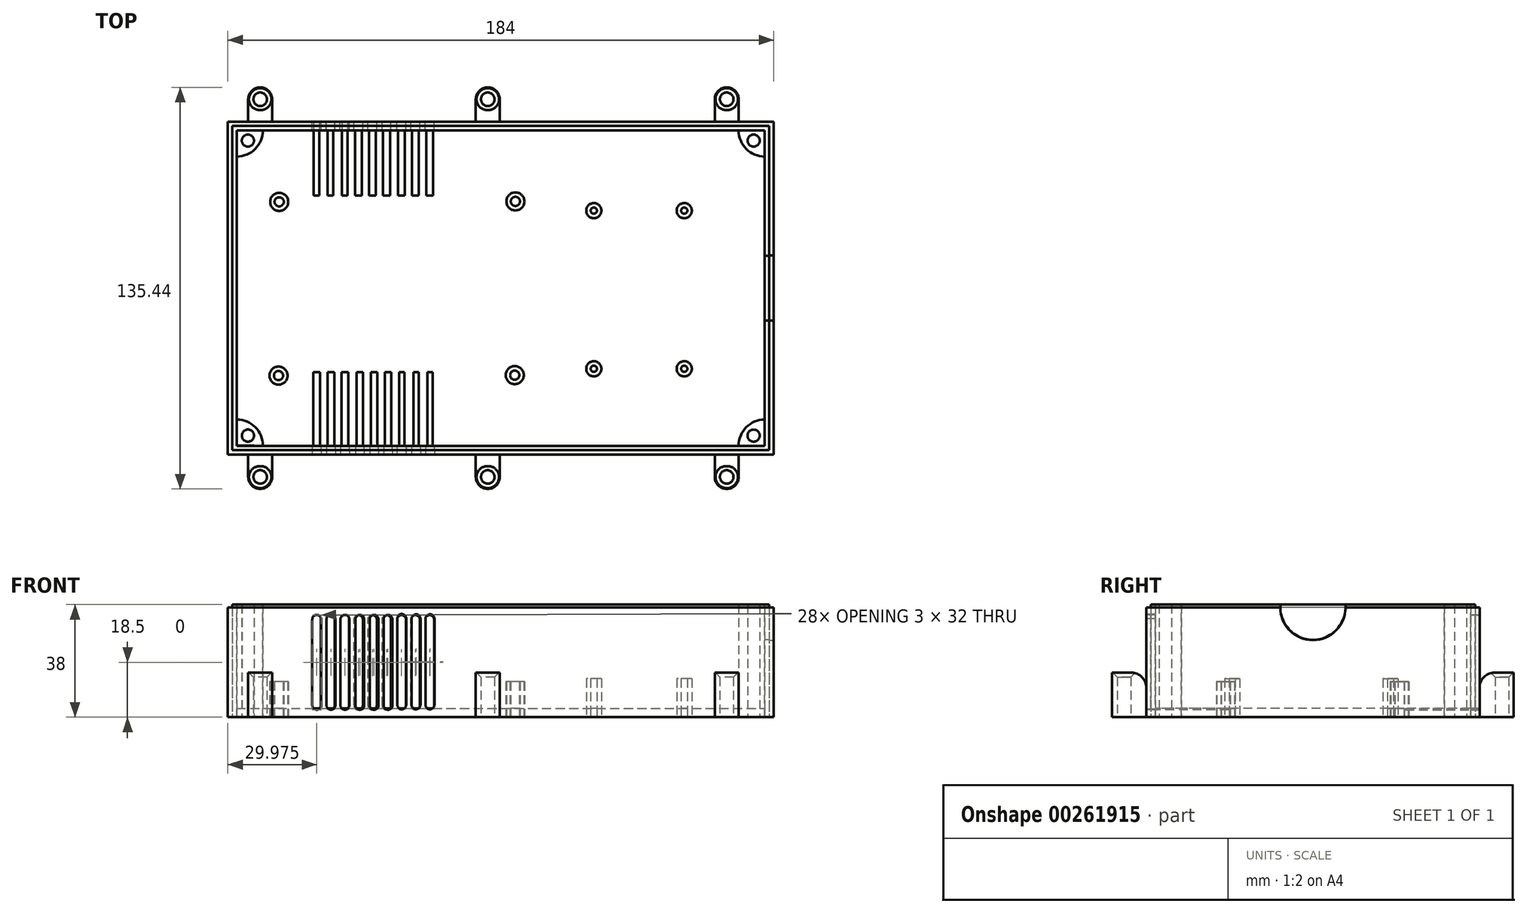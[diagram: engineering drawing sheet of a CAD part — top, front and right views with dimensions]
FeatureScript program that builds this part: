
annotation { "Feature Type Name" : "Feature", "Feature Type Description" : "" }
export const myFeature = defineFeature(function(context is Context, id is Id, definition is map)
    precondition{}
    {
        {
            var Q0;
            Q0=qCreatedBy(makeId("Top.planeOp"),FACE);
            var sketch = newSketch(context, id + "F0", { "sketchPlane" : qUnion([Q0])});
            skLineSegment(sketch, "E0.bottom", {"start": v(-92, 56.17) * mm, "end": v(92, 56.17) * mm});
            skLineSegment(sketch, "E0.top", {"start": v(-92, -56.17) * mm, "end": v(92, -56.17) * mm});
            skLineSegment(sketch, "E0.left", {"start": v(-92, 56.17) * mm, "end": v(-92, -56.17) * mm});
            skLineSegment(sketch, "E0.right", {"start": v(92, 56.17) * mm, "end": v(92, -56.17) * mm});
            skPoint(sketch, "E0.middle", {"position": v(0, 0) * mm});
            skLineSegment(sketch, "E1.0", {"start": v(-89, 53.17) * mm, "end": v(89, 53.17) * mm});
            skLineSegment(sketch, "E1.1", {"start": v(-89, 53.17) * mm, "end": v(-89, -53.17) * mm});
            skLineSegment(sketch, "E1.2", {"start": v(-89, -53.17) * mm, "end": v(89, -53.17) * mm});
            skLineSegment(sketch, "E1.3", {"start": v(89, 53.17) * mm, "end": v(89, -53.17) * mm});
            skLineSegment(sketch, "E2.0", {"start": v(-90.5, 54.67) * mm, "end": v(90.5, 54.67) * mm});
            skLineSegment(sketch, "E2.1", {"start": v(-90.5, 54.67) * mm, "end": v(-90.5, -54.67) * mm});
            skLineSegment(sketch, "E2.2", {"start": v(-90.5, -54.67) * mm, "end": v(90.5, -54.67) * mm});
            skLineSegment(sketch, "E2.3", {"start": v(90.5, 54.67) * mm, "end": v(90.5, -54.67) * mm});
            skSolve(sketch);
        }
        {
            var Q0;
            Q0=makeQuery(id+"F0.imprint","IMPRINT",FACE,{"disambiguationData":[TD([[makeQuery(id+"F0.imprint","IMPRINT",EDGE,{"derivedFrom":sQuery(id+"F0.wireOp",EDGE,"E1.0")}),-1.0]])]});
            var sketch = newSketch(context, id + "F1", { "sketchPlane" : qUnion([Q0])});
            skCircle(sketch, "E3", {"center": v(-85.23, 49.75) * mm, "radius": 2.05 * mm});
            skLineSegment(sketch, "E4", {"start": v(-83.13, 53.17) * mm, "end": v(-89, 53.17) * mm});
            skLineSegment(sketch, "E5", {"start": v(-89, 53.17) * mm, "end": v(-89, 50.23) * mm});
            skLineSegment(sketch, "E6.MirrorCS", {"start": v(-89, 47.29) * mm, "end": v(-89, 50.23) * mm});
            skLineSegment(sketch, "E7.MirrorCS", {"start": v(-89, 47.29) * mm, "end": v(-89, 44.34) * mm});
            skLineSegment(sketch, "E8", {"start": v(-80.2, 53.17) * mm, "end": v(-83.13, 53.17) * mm});
            skArc(sketch, "E9", {"start": v(-89, 44.34) * mm, "mid": v(-82.77, 46.94) * mm, "end": v(-80.2, 53.17) * mm});
            skLineSegment(sketch, "E10.MirrorCS", {"start": v(83.13, 53.17) * mm, "end": v(89, 53.17) * mm});
            skCircle(sketch, "E11.MirrorC", {"center": v(85.23, 49.75) * mm, "radius": 2.05 * mm});
            skLineSegment(sketch, "E12.MirrorCS", {"start": v(89, 53.17) * mm, "end": v(89, 50.23) * mm});
            skLineSegment(sketch, "E13.MirrorCS", {"start": v(80.2, 53.17) * mm, "end": v(83.13, 53.17) * mm});
            skLineSegment(sketch, "E14.MirrorCS", {"start": v(89, 47.29) * mm, "end": v(89, 50.23) * mm});
            skLineSegment(sketch, "E15.MirrorCS", {"start": v(89, 47.29) * mm, "end": v(89, 44.34) * mm});
            skArc(sketch, "E16.MirrorCS", {"start": v(89, 44.34) * mm, "mid": v(82.77, 46.94) * mm, "end": v(80.2, 53.17) * mm});
            skLineSegment(sketch, "E17.MirrorCS", {"start": v(-88.98, -53.17) * mm, "end": v(-88.98, -50.22) * mm});
            skLineSegment(sketch, "E18.MirrorCS", {"start": v(-88.98, -47.28) * mm, "end": v(-88.98, -50.22) * mm});
            skLineSegment(sketch, "E19.MirrorCS", {"start": v(-88.98, -47.28) * mm, "end": v(-88.98, -44.34) * mm});
            skLineSegment(sketch, "E20.MirrorCS", {"start": v(-80.17, -53.17) * mm, "end": v(-83.1, -53.17) * mm});
            skLineSegment(sketch, "E21.MirrorCS", {"start": v(80.2, -53.17) * mm, "end": v(83.13, -53.17) * mm});
            skLineSegment(sketch, "E22.MirrorCS", {"start": v(89, -53.17) * mm, "end": v(89, -50.23) * mm});
            skLineSegment(sketch, "E23.MirrorCS", {"start": v(89, -47.29) * mm, "end": v(89, -50.23) * mm});
            skLineSegment(sketch, "E24.MirrorCS", {"start": v(89, -47.29) * mm, "end": v(89, -44.34) * mm});
            skCircle(sketch, "E25.MirrorC", {"center": v(85.23, -49.75) * mm, "radius": 2.05 * mm});
            skLineSegment(sketch, "E26.MirrorCS", {"start": v(-83.1, -53.17) * mm, "end": v(-88.98, -53.17) * mm});
            skLineSegment(sketch, "E27.MirrorCS", {"start": v(83.13, -53.17) * mm, "end": v(89, -53.17) * mm});
            skArc(sketch, "E28.MirrorCS", {"start": v(89, -44.34) * mm, "mid": v(82.77, -46.94) * mm, "end": v(80.2, -53.17) * mm});
            skArc(sketch, "E29.MirrorCS", {"start": v(-88.98, -44.34) * mm, "mid": v(-82.75, -46.93) * mm, "end": v(-80.17, -53.17) * mm});
            skCircle(sketch, "E30.MirrorC", {"center": v(-85.21, -49.75) * mm, "radius": 2.05 * mm});
            skSolve(sketch);
        }
        {
            var Q0;
            Q0=makeQuery(id+"F0.imprint","IMPRINT",FACE,{"disambiguationData":[TD([[makeQuery(id+"F0.imprint","IMPRINT",EDGE,{"derivedFrom":sQuery(id+"F0.wireOp",EDGE,"E1.0")}),-1.0]])]});
            var sketch = newSketch(context, id + "F2", { "sketchPlane" : qUnion([Q0])});
            skLineSegment(sketch, "E31", {"start": v(-85.12, 56.17) * mm, "end": v(-85.12, 63.69) * mm});
            skLineSegment(sketch, "E32", {"start": v(-77.06, 63.69) * mm, "end": v(-77.06, 56.17) * mm});
            skArc(sketch, "E33", {"start": v(-77.06, 63.69) * mm, "mid": v(-81.09, 67.72) * mm, "end": v(-85.12, 63.69) * mm});
            skCircle(sketch, "E34", {"center": v(-81.09, 63.69) * mm, "radius": 2.28 * mm});
            skLineSegment(sketch, "E35", {"start": v(72.14, 56.17) * mm, "end": v(72.14, 63.69) * mm});
            skLineSegment(sketch, "E36", {"start": v(80.2, 63.69) * mm, "end": v(80.2, 56.17) * mm});
            skArc(sketch, "E37", {"start": v(80.2, 63.69) * mm, "mid": v(76.16, 67.72) * mm, "end": v(72.14, 63.69) * mm});
            skCircle(sketch, "E38", {"center": v(76.16, 63.69) * mm, "radius": 2.28 * mm});
            skLineSegment(sketch, "E39", {"start": v(-77.06, -56.17) * mm, "end": v(-77.06, -63.69) * mm});
            skLineSegment(sketch, "E40", {"start": v(-85.12, -63.69) * mm, "end": v(-85.12, -56.17) * mm});
            skArc(sketch, "E41", {"start": v(-85.12, -63.69) * mm, "mid": v(-81.09, -67.72) * mm, "end": v(-77.06, -63.69) * mm});
            skCircle(sketch, "E42", {"center": v(-81.09, -63.69) * mm, "radius": 2.28 * mm});
            skLineSegment(sketch, "E43", {"start": v(80.2, -56.17) * mm, "end": v(80.2, -63.69) * mm});
            skLineSegment(sketch, "E44", {"start": v(72.14, -63.69) * mm, "end": v(72.14, -56.17) * mm});
            skArc(sketch, "E45", {"start": v(72.14, -63.69) * mm, "mid": v(76.16, -67.72) * mm, "end": v(80.2, -63.69) * mm});
            skCircle(sketch, "E46", {"center": v(76.16, -63.69) * mm, "radius": 2.28 * mm});
            skLineSegment(sketch, "E47", {"start": v(-85.12, 56.17) * mm, "end": v(-77.06, 56.17) * mm});
            skLineSegment(sketch, "E48", {"start": v(72.14, 56.17) * mm, "end": v(80.2, 56.17) * mm});
            skLineSegment(sketch, "E49", {"start": v(72.14, -56.17) * mm, "end": v(80.2, -56.17) * mm});
            skLineSegment(sketch, "E50", {"start": v(-85.12, -56.17) * mm, "end": v(-77.06, -56.17) * mm});
            skLineSegment(sketch, "E51", {"start": v(-8.4, 56.17) * mm, "end": v(-8.4, 63.69) * mm});
            skLineSegment(sketch, "E52", {"start": v(-0.35, 63.69) * mm, "end": v(-0.35, 56.17) * mm});
            skArc(sketch, "E53", {"start": v(-0.35, 63.69) * mm, "mid": v(-4.37, 67.72) * mm, "end": v(-8.4, 63.69) * mm});
            skCircle(sketch, "E54", {"center": v(-4.37, 63.69) * mm, "radius": 2.28 * mm});
            skLineSegment(sketch, "E55", {"start": v(-0.35, -56.17) * mm, "end": v(-0.35, -63.69) * mm});
            skLineSegment(sketch, "E56", {"start": v(-8.4, -63.69) * mm, "end": v(-8.4, -56.17) * mm});
            skArc(sketch, "E57", {"start": v(-8.4, -63.69) * mm, "mid": v(-4.37, -67.72) * mm, "end": v(-0.35, -63.69) * mm});
            skCircle(sketch, "E58", {"center": v(-4.37, -63.69) * mm, "radius": 2.28 * mm});
            skLineSegment(sketch, "E59", {"start": v(-8.4, 56.17) * mm, "end": v(-0.35, 56.17) * mm});
            skLineSegment(sketch, "E60", {"start": v(-8.4, -56.17) * mm, "end": v(-0.35, -56.17) * mm});
            skSolve(sketch);
        }
        {
            var Q0;
            Q0=makeQuery(id+"F0.imprint","IMPRINT",FACE,{"disambiguationData":[TD([[makeQuery(id+"F0.imprint","IMPRINT",EDGE,{"derivedFrom":sQuery(id+"F0.wireOp",EDGE,"E1.0")}),-1.0]])]});
            var sketch = newSketch(context, id + "F3", { "sketchPlane" : qUnion([Q0])});
            skCircle(sketch, "E61", {"center": v(-74.92, -29.5) * mm, "radius": 1.55 * mm});
            skCircle(sketch, "E62", {"center": v(-74.68, 29.1) * mm, "radius": 1.55 * mm});
            skCircle(sketch, "E63", {"center": v(4.94, 29.25) * mm, "radius": 1.55 * mm});
            skCircle(sketch, "E64", {"center": v(4.7, -29.35) * mm, "radius": 1.55 * mm});
            skCircle(sketch, "E65.0", {"center": v(-74.92, -29.5) * mm, "radius": 3.05 * mm});
            skCircle(sketch, "E66.0", {"center": v(-74.68, 29.1) * mm, "radius": 3.05 * mm});
            skCircle(sketch, "E67.0", {"center": v(4.7, -29.35) * mm, "radius": 3.05 * mm});
            skCircle(sketch, "E68.0", {"center": v(4.94, 29.25) * mm, "radius": 3.05 * mm});
            skSolve(sketch);
        }
        {
            var Q0;
            Q0 = qSketchRegion(id + "F3", true);
            extrude(context, id + "F4", {"entities" : qUnion([Q0]), "depth" : 12 * mm});
        }
        {
            var Q0;
            Q0=makeQuery(id+"F3.imprint","IMPRINT",FACE,{"disambiguationData":[TD([[makeQuery(id+"F3.imprint","IMPRINT",EDGE,{"derivedFrom":sQuery(id+"F3.wireOp",EDGE,"E62")}),1.0]])]});
            var Q1;
            Q1=makeQuery(id+"F3.imprint","IMPRINT",FACE,{"disambiguationData":[TD([[makeQuery(id+"F3.imprint","IMPRINT",EDGE,{"derivedFrom":sQuery(id+"F3.wireOp",EDGE,"E63")}),1.0]])]});
            var Q2;
            Q2=makeQuery(id+"F3.imprint","IMPRINT",FACE,{"disambiguationData":[TD([[makeQuery(id+"F3.imprint","IMPRINT",EDGE,{"derivedFrom":sQuery(id+"F3.wireOp",EDGE,"E61")}),1.0]])]});
            var Q3;
            Q3=makeQuery(id+"F3.imprint","IMPRINT",FACE,{"disambiguationData":[TD([[makeQuery(id+"F3.imprint","IMPRINT",EDGE,{"derivedFrom":sQuery(id+"F3.wireOp",EDGE,"E64")}),1.0]])]});
            extrude(context, id + "F5", {"entities" : qUnion([Q0, Q1, Q2, Q3]), "depth" : 3 * mm});
        }
        {
            var Q0;
            Q0=makeQuery(id+"F0.imprint","IMPRINT",FACE,{"disambiguationData":[TD([[makeQuery(id+"F0.imprint","IMPRINT",EDGE,{"derivedFrom":sQuery(id+"F0.wireOp",EDGE,"E1.0")}),-1.0]])]});
            var sketch = newSketch(context, id + "F6", { "sketchPlane" : qUnion([Q0])});
            skCircle(sketch, "E69", {"center": v(31.37, 26.14) * mm, "radius": 1.05 * mm});
            skCircle(sketch, "E70", {"center": v(61.85, 26.14) * mm, "radius": 1.05 * mm});
            skCircle(sketch, "E71", {"center": v(61.85, -27.2) * mm, "radius": 1.05 * mm});
            skCircle(sketch, "E72", {"center": v(31.37, -27.2) * mm, "radius": 1.05 * mm});
            skCircle(sketch, "E73.0", {"center": v(31.37, 26.14) * mm, "radius": 2.55 * mm});
            skCircle(sketch, "E74.0", {"center": v(61.85, 26.14) * mm, "radius": 2.55 * mm});
            skCircle(sketch, "E75.0", {"center": v(31.37, -27.2) * mm, "radius": 2.55 * mm});
            skCircle(sketch, "E76.0", {"center": v(61.85, -27.2) * mm, "radius": 2.55 * mm});
            skSolve(sketch);
        }
        {
            var Q0;
            Q0=makeQuery(id+"F0.imprint","IMPRINT",FACE,{"disambiguationData":[TD([[makeQuery(id+"F0.imprint","IMPRINT",EDGE,{"derivedFrom":sQuery(id+"F0.wireOp",EDGE,"E0.bottom")}),-1.0]])]});
            extrude(context, id + "F7", {"entities" : qUnion([Q0]), "depth" : 37 * mm});
        }
        {
            var Q0;
            Q0=makeQuery(id+"F2.imprint","IMPRINT",FACE,{"disambiguationData":[TD([[makeQuery(id+"F2.imprint","IMPRINT",EDGE,{"derivedFrom":sQuery(id+"F2.wireOp",EDGE,"E31")}),-1.0]])]});
            var Q1;
            Q1=makeQuery(id+"F2.imprint","IMPRINT",FACE,{"disambiguationData":[TD([[makeQuery(id+"F2.imprint","IMPRINT",EDGE,{"derivedFrom":sQuery(id+"F2.wireOp",EDGE,"E35")}),-1.0]])]});
            var Q2;
            Q2=makeQuery(id+"F2.imprint","IMPRINT",FACE,{"disambiguationData":[TD([[makeQuery(id+"F2.imprint","IMPRINT",EDGE,{"derivedFrom":sQuery(id+"F2.wireOp",EDGE,"E39")}),-1.0]])]});
            var Q3;
            Q3=makeQuery(id+"F2.imprint","IMPRINT",FACE,{"disambiguationData":[TD([[makeQuery(id+"F2.imprint","IMPRINT",EDGE,{"derivedFrom":sQuery(id+"F2.wireOp",EDGE,"E43")}),-1.0]])]});
            var Q4;
            Q4=makeQuery(id+"F2.imprint","IMPRINT",FACE,{"disambiguationData":[TD([[makeQuery(id+"F2.imprint","IMPRINT",EDGE,{"derivedFrom":sQuery(id+"F2.wireOp",EDGE,"E55")}),-1.0]])]});
            var Q5;
            Q5=makeQuery(id+"F2.imprint","IMPRINT",FACE,{"disambiguationData":[TD([[makeQuery(id+"F2.imprint","IMPRINT",EDGE,{"derivedFrom":sQuery(id+"F2.wireOp",EDGE,"E51")}),-1.0]])]});
            extrude(context, id + "F8", {"entities" : qUnion([Q0, Q1, Q2, Q3, Q4, Q5]), "operationType" : NewBodyOperationType.ADD, "depth" : 15 * mm});
        }
        {
            var Q0;
            Q0=makeQuery(id+"F8.opExtrude","CAP_EDGE",EDGE,{"disambiguationData":[OSD([sQuery(id+"F2.wireOp",EDGE,"E34")])],"isStart":false});
            var Q1;
            Q1=makeQuery(id+"F8.opExtrude","CAP_EDGE",EDGE,{"disambiguationData":[OSD([sQuery(id+"F2.wireOp",EDGE,"E38")])],"isStart":false});
            var Q2;
            Q2=makeQuery(id+"F8.opExtrude","CAP_EDGE",EDGE,{"disambiguationData":[OSD([sQuery(id+"F2.wireOp",EDGE,"E46")])],"isStart":false});
            var Q3;
            Q3=makeQuery(id+"F8.opExtrude","CAP_EDGE",EDGE,{"disambiguationData":[OSD([sQuery(id+"F2.wireOp",EDGE,"E42")])],"isStart":false});
            var Q4;
            Q4=makeQuery(id+"F8.opExtrude","CAP_EDGE",EDGE,{"disambiguationData":[OSD([sQuery(id+"F2.wireOp",EDGE,"E54")])],"isStart":false});
            var Q5;
            Q5=makeQuery(id+"F8.opExtrude","CAP_EDGE",EDGE,{"disambiguationData":[OSD([sQuery(id+"F2.wireOp",EDGE,"E58")])],"isStart":false});
            chamfer(context, id + "F9", {"entities" : qUnion([Q0, Q1, Q2, Q3, Q4, Q5]), "width" : 1.5 * mm, "tangentPropagation" : true});
        }
        {
            var Q0;
            Q0=makeQuery(id+"F6.imprint","IMPRINT",FACE,{"disambiguationData":[TD([[makeQuery(id+"F6.imprint","IMPRINT",EDGE,{"derivedFrom":sQuery(id+"F6.wireOp",EDGE,"E72")}),1.0]])]});
            var Q1;
            Q1=makeQuery(id+"F6.imprint","IMPRINT",FACE,{"disambiguationData":[TD([[makeQuery(id+"F6.imprint","IMPRINT",EDGE,{"derivedFrom":sQuery(id+"F6.wireOp",EDGE,"E71")}),1.0]])]});
            var Q2;
            Q2=makeQuery(id+"F6.imprint","IMPRINT",FACE,{"disambiguationData":[TD([[makeQuery(id+"F6.imprint","IMPRINT",EDGE,{"derivedFrom":sQuery(id+"F6.wireOp",EDGE,"E69")}),1.0]])]});
            var Q3;
            Q3=makeQuery(id+"F6.imprint","IMPRINT",FACE,{"disambiguationData":[TD([[makeQuery(id+"F6.imprint","IMPRINT",EDGE,{"derivedFrom":sQuery(id+"F6.wireOp",EDGE,"E70")}),1.0]])]});
            var Q4;
            Q4=sQuery(id+"F6.wireOp",EDGE,"E72");
            var Q5;
            Q5=sQuery(id+"F6.wireOp",EDGE,"E71");
            var Q6;
            Q6=sQuery(id+"F6.wireOp",EDGE,"E70");
            var Q7;
            Q7=sQuery(id+"F6.wireOp",EDGE,"E69");
            extrude(context, id + "F10", {"entities" : qUnion([Q0, Q1, Q2, Q3]), "surfaceEntities" : qUnion([Q4, Q5, Q6, Q7]), "depth" : 3 * mm});
        }
        {
            var Q0;
            Q0 = qSketchRegion(id + "F6", true);
            extrude(context, id + "F11", {"entities" : qUnion([Q0]), "depth" : 13 * mm});
        }
        {
            var Q0;
            Q0=makeQuery(id+"F0.imprint","IMPRINT",FACE,{"disambiguationData":[TD([[makeQuery(id+"F0.imprint","IMPRINT",EDGE,{"derivedFrom":sQuery(id+"F0.wireOp",EDGE,"E1.0")}),-1.0]])]});
            extrude(context, id + "F12", {"entities" : qUnion([Q0]), "depth" : 3 * mm});
        }
        {
            var Q0;
            Q0=makeQuery(id+"F8.opExtrude","CAP_EDGE",EDGE,{"disambiguationData":[OSD([sQuery(id+"F2.wireOp",EDGE,"E48")])],"isStart":false});
            var Q1;
            Q1=makeQuery(id+"F8.boolean.opBoolean","INTERSECT",EDGE,{"derivedFrom":[makeQuery(id+"F7.opExtrude","SWEPT_FACE",FACE,{"disambiguationData":[OSD([sQuery(id+"F0.wireOp",EDGE,"E0.bottom")])]}),makeQuery(id+"F8.opExtrude","CAP_FACE",FACE,{"disambiguationData":[OSD([sQuery(id+"F2.wireOp",EDGE,"E31"),sQuery(id+"F2.wireOp",EDGE,"E32"),sQuery(id+"F2.wireOp",EDGE,"E33"),sQuery(id+"F2.wireOp",EDGE,"E34"),sQuery(id+"F2.wireOp",EDGE,"E47")])],"isStart":false})]});
            var Q2;
            Q2=makeQuery(id+"F8.boolean.opBoolean","INTERSECT",EDGE,{"derivedFrom":[makeQuery(id+"F7.opExtrude","SWEPT_FACE",FACE,{"disambiguationData":[OSD([sQuery(id+"F0.wireOp",EDGE,"E0.top")])]}),makeQuery(id+"F8.opExtrude","CAP_FACE",FACE,{"disambiguationData":[OSD([sQuery(id+"F2.wireOp",EDGE,"E39"),sQuery(id+"F2.wireOp",EDGE,"E40"),sQuery(id+"F2.wireOp",EDGE,"E41"),sQuery(id+"F2.wireOp",EDGE,"E42"),sQuery(id+"F2.wireOp",EDGE,"E50")])],"isStart":false})]});
            var Q3;
            Q3=makeQuery(id+"F8.boolean.opBoolean","INTERSECT",EDGE,{"derivedFrom":[makeQuery(id+"F7.opExtrude","SWEPT_FACE",FACE,{"disambiguationData":[OSD([sQuery(id+"F0.wireOp",EDGE,"E0.top")])]}),makeQuery(id+"F8.opExtrude","CAP_FACE",FACE,{"disambiguationData":[OSD([sQuery(id+"F2.wireOp",EDGE,"E43"),sQuery(id+"F2.wireOp",EDGE,"E44"),sQuery(id+"F2.wireOp",EDGE,"E45"),sQuery(id+"F2.wireOp",EDGE,"E46"),sQuery(id+"F2.wireOp",EDGE,"E49")])],"isStart":false})]});
            var Q4;
            Q4=makeQuery(id+"F8.opExtrude","CAP_EDGE",EDGE,{"disambiguationData":[OSD([sQuery(id+"F2.wireOp",EDGE,"E59")])],"isStart":false});
            var Q5;
            Q5=makeQuery(id+"F8.boolean.opBoolean","INTERSECT",EDGE,{"derivedFrom":[makeQuery(id+"F7.opExtrude","SWEPT_FACE",FACE,{"disambiguationData":[OSD([sQuery(id+"F0.wireOp",EDGE,"E0.top")])]}),makeQuery(id+"F8.opExtrude","CAP_FACE",FACE,{"disambiguationData":[OSD([sQuery(id+"F2.wireOp",EDGE,"E55"),sQuery(id+"F2.wireOp",EDGE,"E56"),sQuery(id+"F2.wireOp",EDGE,"E57"),sQuery(id+"F2.wireOp",EDGE,"E58"),sQuery(id+"F2.wireOp",EDGE,"E60")])],"isStart":false})]});
            var Q6;
            Q6=makeQuery(id+"F8.opExtrude","CAP_EDGE",EDGE,{"disambiguationData":[OSD([sQuery(id+"F2.wireOp",EDGE,"E50")])],"isStart":false});
            var Q7;
            Q7=makeQuery(id+"F8.opExtrude","CAP_EDGE",EDGE,{"disambiguationData":[OSD([sQuery(id+"F2.wireOp",EDGE,"E60")])],"isStart":false});
            var Q8;
            Q8=makeQuery(id+"F8.opExtrude","CAP_EDGE",EDGE,{"disambiguationData":[OSD([sQuery(id+"F2.wireOp",EDGE,"E49")])],"isStart":false});
            var Q9;
            Q9=makeQuery(id+"F8.opExtrude","CAP_EDGE",EDGE,{"disambiguationData":[OSD([sQuery(id+"F2.wireOp",EDGE,"E47")])],"isStart":false});
            fillet(context, id + "F13", {"entities" : qUnion([Q0, Q1, Q2, Q3, Q4, Q5, Q6, Q7, Q8, Q9]), "radius" : 5 * mm, "tangentPropagation" : true, "allowEdgeOverflow" : false});
        }
        {
            var Q0;
            Q0=makeQuery(id+"F7.opExtrude","SWEPT_FACE",FACE,{"disambiguationData":[OSD([sQuery(id+"F0.wireOp",EDGE,"E0.right")])]});
            var sketch = newSketch(context, id + "F14", { "sketchPlane" : qUnion([Q0])});
            skLineSegment(sketch, "E77", {"start": v(0, 0) * mm, "end": v(0, 37) * mm});
            skLineSegment(sketch, "E78", {"start": v(0, 37) * mm, "end": v(0, 18.5) * mm});
            skLineSegment(sketch, "E79", {"start": v(0, 14) * mm, "end": v(0, 18.5) * mm});
            skLineSegment(sketch, "E80", {"start": v(0, 37) * mm, "end": v(0, 21.99) * mm});
            skSolve(sketch);
        }
        {
            var Q0;
            Q0=makeQuery(id+"F0.imprint","IMPRINT",FACE,{"disambiguationData":[TD([[makeQuery(id+"F0.imprint","IMPRINT",EDGE,{"derivedFrom":sQuery(id+"F0.wireOp",EDGE,"E1.0")}),1.0]])]});
            extrude(context, id + "F15", {"entities" : qUnion([Q0]), "depth" : 38 * mm});
        }
        {
            var Q0;
            Q0=sQuery(id+"F14.wireOp",VERTEX,"E80.start");
            var Q1;
            Q1=makeQuery(id+"F7.opExtrude","SWEPT_BODY",BODY,{"disambiguationData":[OSD([sQuery(id+"F0.wireOp",EDGE,"E0.bottom"),sQuery(id+"F0.wireOp",EDGE,"E0.top"),sQuery(id+"F0.wireOp",EDGE,"E0.left"),sQuery(id+"F0.wireOp",EDGE,"E0.right"),sQuery(id+"F0.wireOp",EDGE,"E1.0"),sQuery(id+"F0.wireOp",EDGE,"E1.1"),sQuery(id+"F0.wireOp",EDGE,"E1.2"),sQuery(id+"F0.wireOp",EDGE,"E1.3")])]});
            hole(context, id + "F16", {"style" : HoleStyle.SIMPLE, "endStyle" : HoleEndStyle.BLIND, "holeDiameter" : 22 * mm, "holeDepth" : 12 * mm, "tappedDepth" : 12 * mm, "tapClearance" : 3, "startFromSketch" : true, "locations" : qUnion([Q0]), "scope" : qUnion([Q1])});
        }
        {
            var Q0;
            Q0=makeQuery(id+"F15.opExtrude","SWEPT_FACE",FACE,{"disambiguationData":[OSD([sQuery(id+"F0.wireOp",EDGE,"E1.3")])]});
            var sketch = newSketch(context, id + "F17", { "sketchPlane" : qUnion([Q0])});
            skLineSegment(sketch, "E81", {"start": v(0, -23) * mm, "end": v(0, 12) * mm});
            skLineSegment(sketch, "E82", {"start": v(0, 12) * mm, "end": v(0, -5.5) * mm});
            skLineSegment(sketch, "E83", {"start": v(0, -9) * mm, "end": v(0, -5.5) * mm});
            skLineSegment(sketch, "E84", {"start": v(0, 12) * mm, "end": v(0, -1.01) * mm});
            skLineSegment(sketch, "E85", {"start": v(0, 37.12) * mm, "end": v(-0.2, 22.08) * mm});
            skSolve(sketch);
        }
        {
            var Q0;
            Q0=sQuery(id+"F17.wireOp",VERTEX,"E85.start");
            var Q1;
            Q1=makeQuery(id+"F15.opExtrude","SWEPT_BODY",BODY,{"disambiguationData":[OSD([sQuery(id+"F0.wireOp",EDGE,"E1.0"),sQuery(id+"F0.wireOp",EDGE,"E1.1"),sQuery(id+"F0.wireOp",EDGE,"E1.2"),sQuery(id+"F0.wireOp",EDGE,"E1.3"),sQuery(id+"F0.wireOp",EDGE,"E2.0"),sQuery(id+"F0.wireOp",EDGE,"E2.1"),sQuery(id+"F0.wireOp",EDGE,"E2.2"),sQuery(id+"F0.wireOp",EDGE,"E2.3")])]});
            hole(context, id + "F18", {"style" : HoleStyle.SIMPLE, "endStyle" : HoleEndStyle.BLIND, "holeDiameter" : 22 * mm, "holeDepth" : 12 * mm, "tappedDepth" : 12 * mm, "tapClearance" : 3, "startFromSketch" : true, "locations" : qUnion([Q0]), "scope" : qUnion([Q1])});
        }
        {
            var Q0;
            Q0=makeQuery(id+"F7.opExtrude","SWEPT_FACE",FACE,{"disambiguationData":[OSD([sQuery(id+"F0.wireOp",EDGE,"E0.top")])]});
            var sketch = newSketch(context, id + "F19", { "sketchPlane" : qUnion([Q0])});
            skLineSegment(sketch, "E86", {"start": v(-60.52, 4) * mm, "end": v(-60.52, 33) * mm});
            skLineSegment(sketch, "E87", {"start": v(-63.52, 4) * mm, "end": v(-63.52, 33) * mm});
            skArc(sketch, "E88", {"start": v(-60.52, 33) * mm, "mid": v(-62.02, 34.5) * mm, "end": v(-63.52, 33) * mm});
            skArc(sketch, "E89", {"start": v(-63.52, 4) * mm, "mid": v(-62.02, 2.5) * mm, "end": v(-60.52, 4) * mm});
            skLineSegment(sketch, "E90", {"start": v(-55.72, 4) * mm, "end": v(-55.72, 33) * mm});
            skLineSegment(sketch, "E91", {"start": v(-58.72, 4) * mm, "end": v(-58.72, 33) * mm});
            skArc(sketch, "E92", {"start": v(-55.72, 33) * mm, "mid": v(-57.22, 34.5) * mm, "end": v(-58.72, 33) * mm});
            skArc(sketch, "E93", {"start": v(-58.72, 4) * mm, "mid": v(-57.22, 2.5) * mm, "end": v(-55.72, 4) * mm});
            skLineSegment(sketch, "E94", {"start": v(-51.02, 4) * mm, "end": v(-51.02, 33) * mm});
            skLineSegment(sketch, "E95", {"start": v(-54.02, 4) * mm, "end": v(-54.02, 33) * mm});
            skArc(sketch, "E96", {"start": v(-51.02, 33) * mm, "mid": v(-52.52, 34.5) * mm, "end": v(-54.02, 33) * mm});
            skArc(sketch, "E97", {"start": v(-54.02, 4) * mm, "mid": v(-52.52, 2.5) * mm, "end": v(-51.02, 4) * mm});
            skLineSegment(sketch, "E98", {"start": v(-46, 4) * mm, "end": v(-46, 33) * mm});
            skLineSegment(sketch, "E99", {"start": v(-49, 4) * mm, "end": v(-49, 33) * mm});
            skArc(sketch, "E100", {"start": v(-46, 33) * mm, "mid": v(-47.5, 34.5) * mm, "end": v(-49, 33) * mm});
            skArc(sketch, "E101", {"start": v(-49, 4) * mm, "mid": v(-47.5, 2.5) * mm, "end": v(-46, 4) * mm});
            skLineSegment(sketch, "E102", {"start": v(-41.2, 4) * mm, "end": v(-41.2, 33) * mm});
            skLineSegment(sketch, "E103", {"start": v(-44.2, 4) * mm, "end": v(-44.2, 33) * mm});
            skArc(sketch, "E104", {"start": v(-41.2, 33) * mm, "mid": v(-42.7, 34.5) * mm, "end": v(-44.2, 33) * mm});
            skArc(sketch, "E105", {"start": v(-44.2, 4) * mm, "mid": v(-42.7, 2.5) * mm, "end": v(-41.2, 4) * mm});
            skLineSegment(sketch, "E106", {"start": v(-36.5, 4) * mm, "end": v(-36.5, 33) * mm});
            skLineSegment(sketch, "E107", {"start": v(-39.5, 4) * mm, "end": v(-39.5, 33) * mm});
            skArc(sketch, "E108", {"start": v(-36.5, 33) * mm, "mid": v(-38, 34.5) * mm, "end": v(-39.5, 33) * mm});
            skArc(sketch, "E109", {"start": v(-39.5, 4) * mm, "mid": v(-38, 2.5) * mm, "end": v(-36.5, 4) * mm});
            skLineSegment(sketch, "E110", {"start": v(-31.87, 4.2) * mm, "end": v(-31.87, 33.2) * mm});
            skLineSegment(sketch, "E111", {"start": v(-34.87, 4.2) * mm, "end": v(-34.87, 33.2) * mm});
            skArc(sketch, "E112", {"start": v(-31.87, 33.2) * mm, "mid": v(-33.37, 34.7) * mm, "end": v(-34.87, 33.2) * mm});
            skArc(sketch, "E113", {"start": v(-34.87, 4.2) * mm, "mid": v(-33.37, 2.7) * mm, "end": v(-31.87, 4.2) * mm});
            skLineSegment(sketch, "E114", {"start": v(-27.07, 4.2) * mm, "end": v(-27.07, 33.2) * mm});
            skLineSegment(sketch, "E115", {"start": v(-30.07, 4.2) * mm, "end": v(-30.07, 33.2) * mm});
            skArc(sketch, "E116", {"start": v(-27.07, 33.2) * mm, "mid": v(-28.57, 34.7) * mm, "end": v(-30.07, 33.2) * mm});
            skArc(sketch, "E117", {"start": v(-30.07, 4.2) * mm, "mid": v(-28.57, 2.7) * mm, "end": v(-27.07, 4.2) * mm});
            skLineSegment(sketch, "E118", {"start": v(-22.37, 4.2) * mm, "end": v(-22.37, 33.2) * mm});
            skLineSegment(sketch, "E119", {"start": v(-25.37, 4.2) * mm, "end": v(-25.37, 33.2) * mm});
            skArc(sketch, "E120", {"start": v(-22.37, 33.2) * mm, "mid": v(-23.87, 34.7) * mm, "end": v(-25.37, 33.2) * mm});
            skArc(sketch, "E121", {"start": v(-25.37, 4.2) * mm, "mid": v(-23.87, 2.7) * mm, "end": v(-22.37, 4.2) * mm});
            skSolve(sketch);
        }
        {
            var Q0;
            Q0=makeQuery(id+"F15.opExtrude","SWEPT_FACE",FACE,{"disambiguationData":[OSD([sQuery(id+"F0.wireOp",EDGE,"E1.2")])]});
            var sketch = newSketch(context, id + "F20", { "sketchPlane" : qUnion([Q0])});
            skLineSegment(sketch, "E122", {"start": v(25.37, 4.2) * mm, "end": v(25.37, 33.2) * mm});
            skLineSegment(sketch, "E123", {"start": v(22.37, 4.2) * mm, "end": v(22.37, 33.2) * mm});
            skArc(sketch, "E124", {"start": v(25.37, 33.2) * mm, "mid": v(23.87, 34.7) * mm, "end": v(22.37, 33.2) * mm});
            skArc(sketch, "E125", {"start": v(22.37, 4.2) * mm, "mid": v(23.87, 2.7) * mm, "end": v(25.37, 4.2) * mm});
            skLineSegment(sketch, "E126", {"start": v(30.06, 4.2) * mm, "end": v(30.06, 33.2) * mm});
            skLineSegment(sketch, "E127", {"start": v(27.06, 4.2) * mm, "end": v(27.06, 33.2) * mm});
            skArc(sketch, "E128", {"start": v(30.06, 33.2) * mm, "mid": v(28.56, 34.7) * mm, "end": v(27.06, 33.2) * mm});
            skArc(sketch, "E129", {"start": v(27.06, 4.2) * mm, "mid": v(28.56, 2.7) * mm, "end": v(30.06, 4.2) * mm});
            skLineSegment(sketch, "E130", {"start": v(34.87, 4.3) * mm, "end": v(34.87, 33.3) * mm});
            skLineSegment(sketch, "E131", {"start": v(31.87, 4.3) * mm, "end": v(31.87, 33.3) * mm});
            skArc(sketch, "E132", {"start": v(34.87, 33.3) * mm, "mid": v(33.37, 34.8) * mm, "end": v(31.87, 33.3) * mm});
            skArc(sketch, "E133", {"start": v(31.87, 4.3) * mm, "mid": v(33.37, 2.8) * mm, "end": v(34.87, 4.3) * mm});
            skLineSegment(sketch, "E134", {"start": v(39.5, 4) * mm, "end": v(39.5, 33) * mm});
            skLineSegment(sketch, "E135", {"start": v(36.5, 4) * mm, "end": v(36.5, 33) * mm});
            skArc(sketch, "E136", {"start": v(39.5, 33) * mm, "mid": v(38, 34.5) * mm, "end": v(36.5, 33) * mm});
            skArc(sketch, "E137", {"start": v(36.5, 4) * mm, "mid": v(38, 2.5) * mm, "end": v(39.5, 4) * mm});
            skLineSegment(sketch, "E138", {"start": v(44.2, 4) * mm, "end": v(44.2, 33) * mm});
            skLineSegment(sketch, "E139", {"start": v(41.2, 4) * mm, "end": v(41.2, 33) * mm});
            skArc(sketch, "E140", {"start": v(44.2, 33) * mm, "mid": v(42.7, 34.5) * mm, "end": v(41.2, 33) * mm});
            skArc(sketch, "E141", {"start": v(41.2, 4) * mm, "mid": v(42.7, 2.5) * mm, "end": v(44.2, 4) * mm});
            skLineSegment(sketch, "E142", {"start": v(49, 4) * mm, "end": v(49, 33) * mm});
            skLineSegment(sketch, "E143", {"start": v(46, 4) * mm, "end": v(46, 33) * mm});
            skArc(sketch, "E144", {"start": v(49, 33) * mm, "mid": v(47.5, 34.5) * mm, "end": v(46, 33) * mm});
            skArc(sketch, "E145", {"start": v(46, 4) * mm, "mid": v(47.5, 2.5) * mm, "end": v(49, 4) * mm});
            skLineSegment(sketch, "E146", {"start": v(54.03, 4) * mm, "end": v(54.03, 33) * mm});
            skLineSegment(sketch, "E147", {"start": v(51.03, 4) * mm, "end": v(51.03, 33) * mm});
            skArc(sketch, "E148", {"start": v(54.03, 33) * mm, "mid": v(52.53, 34.5) * mm, "end": v(51.03, 33) * mm});
            skArc(sketch, "E149", {"start": v(51.03, 4) * mm, "mid": v(52.53, 2.5) * mm, "end": v(54.03, 4) * mm});
            skLineSegment(sketch, "E150", {"start": v(58.73, 4) * mm, "end": v(58.73, 33) * mm});
            skLineSegment(sketch, "E151", {"start": v(55.73, 4) * mm, "end": v(55.73, 33) * mm});
            skArc(sketch, "E152", {"start": v(58.73, 33) * mm, "mid": v(57.23, 34.5) * mm, "end": v(55.73, 33) * mm});
            skArc(sketch, "E153", {"start": v(55.73, 4) * mm, "mid": v(57.23, 2.5) * mm, "end": v(58.73, 4) * mm});
            skLineSegment(sketch, "E154", {"start": v(63.53, 4) * mm, "end": v(63.53, 33) * mm});
            skLineSegment(sketch, "E155", {"start": v(60.53, 4) * mm, "end": v(60.53, 33) * mm});
            skArc(sketch, "E156", {"start": v(63.53, 33) * mm, "mid": v(62.03, 34.5) * mm, "end": v(60.53, 33) * mm});
            skArc(sketch, "E157", {"start": v(60.53, 4) * mm, "mid": v(62.03, 2.5) * mm, "end": v(63.53, 4) * mm});
            skSolve(sketch);
        }
        {
            var Q0;
            Q0=makeQuery(id+"F19.imprint","IMPRINT",FACE,{"disambiguationData":[TD([[makeQuery(id+"F19.imprint","IMPRINT",EDGE,{"derivedFrom":sQuery(id+"F19.wireOp",EDGE,"E86")}),1.0]])]});
            var Q1;
            Q1=makeQuery(id+"F19.imprint","IMPRINT",FACE,{"disambiguationData":[TD([[makeQuery(id+"F19.imprint","IMPRINT",EDGE,{"derivedFrom":sQuery(id+"F19.wireOp",EDGE,"E90")}),1.0]])]});
            var Q2;
            Q2=makeQuery(id+"F19.imprint","IMPRINT",FACE,{"disambiguationData":[TD([[makeQuery(id+"F19.imprint","IMPRINT",EDGE,{"derivedFrom":sQuery(id+"F19.wireOp",EDGE,"E94")}),1.0]])]});
            var Q3;
            Q3=makeQuery(id+"F19.imprint","IMPRINT",FACE,{"disambiguationData":[TD([[makeQuery(id+"F19.imprint","IMPRINT",EDGE,{"derivedFrom":sQuery(id+"F19.wireOp",EDGE,"E98")}),1.0]])]});
            var Q4;
            Q4=makeQuery(id+"F19.imprint","IMPRINT",FACE,{"disambiguationData":[TD([[makeQuery(id+"F19.imprint","IMPRINT",EDGE,{"derivedFrom":sQuery(id+"F19.wireOp",EDGE,"E102")}),1.0]])]});
            var Q5;
            Q5=makeQuery(id+"F19.imprint","IMPRINT",FACE,{"disambiguationData":[TD([[makeQuery(id+"F19.imprint","IMPRINT",EDGE,{"derivedFrom":sQuery(id+"F19.wireOp",EDGE,"E106")}),1.0]])]});
            var Q6;
            Q6=makeQuery(id+"F19.imprint","IMPRINT",FACE,{"disambiguationData":[TD([[makeQuery(id+"F19.imprint","IMPRINT",EDGE,{"derivedFrom":sQuery(id+"F19.wireOp",EDGE,"E110")}),1.0]])]});
            var Q7;
            Q7=makeQuery(id+"F19.imprint","IMPRINT",FACE,{"disambiguationData":[TD([[makeQuery(id+"F19.imprint","IMPRINT",EDGE,{"derivedFrom":sQuery(id+"F19.wireOp",EDGE,"E114")}),1.0]])]});
            var Q8;
            Q8=makeQuery(id+"F19.imprint","IMPRINT",FACE,{"disambiguationData":[TD([[makeQuery(id+"F19.imprint","IMPRINT",EDGE,{"derivedFrom":sQuery(id+"F19.wireOp",EDGE,"E118")}),1.0]])]});
            extrude(context, id + "F21", {"entities" : qUnion([Q0, Q1, Q2, Q3, Q4, Q5, Q6, Q7, Q8]), "operationType" : NewBodyOperationType.REMOVE, "oppositeDirection" : true, "depth" : 27.8 * mm});
        }
        {
            var Q0;
            Q0 = qSketchRegion(id + "F20", true);
            extrude(context, id + "F22", {"entities" : qUnion([Q0]), "operationType" : NewBodyOperationType.REMOVE, "oppositeDirection" : true, "depth" : 25 * mm});
        }
        {
            var Q0;
            Q0=makeQuery(id+"F7.opExtrude","SWEPT_FACE",FACE,{"disambiguationData":[OSD([sQuery(id+"F0.wireOp",EDGE,"E0.bottom")])]});
            var sketch = newSketch(context, id + "F23", { "sketchPlane" : qUnion([Q0])});
            skLineSegment(sketch, "E158", {"start": v(25.48, 3.95) * mm, "end": v(25.48, 32.95) * mm});
            skLineSegment(sketch, "E159", {"start": v(22.48, 3.95) * mm, "end": v(22.48, 32.95) * mm});
            skArc(sketch, "E160", {"start": v(25.48, 32.95) * mm, "mid": v(23.98, 34.45) * mm, "end": v(22.48, 32.95) * mm});
            skArc(sketch, "E161", {"start": v(22.48, 3.95) * mm, "mid": v(23.98, 2.45) * mm, "end": v(25.48, 3.95) * mm});
            skLineSegment(sketch, "E162", {"start": v(30.28, 3.95) * mm, "end": v(30.28, 32.95) * mm});
            skLineSegment(sketch, "E163", {"start": v(27.28, 3.95) * mm, "end": v(27.28, 32.95) * mm});
            skArc(sketch, "E164", {"start": v(30.28, 32.95) * mm, "mid": v(28.78, 34.45) * mm, "end": v(27.28, 32.95) * mm});
            skArc(sketch, "E165", {"start": v(27.28, 3.95) * mm, "mid": v(28.78, 2.45) * mm, "end": v(30.28, 3.95) * mm});
            skLineSegment(sketch, "E166", {"start": v(34.98, 3.95) * mm, "end": v(34.98, 32.95) * mm});
            skLineSegment(sketch, "E167", {"start": v(31.98, 3.95) * mm, "end": v(31.98, 32.95) * mm});
            skArc(sketch, "E168", {"start": v(34.98, 32.95) * mm, "mid": v(33.48, 34.45) * mm, "end": v(31.98, 32.95) * mm});
            skArc(sketch, "E169", {"start": v(31.98, 3.95) * mm, "mid": v(33.48, 2.45) * mm, "end": v(34.98, 3.95) * mm});
            skLineSegment(sketch, "E170", {"start": v(40, 3.95) * mm, "end": v(40, 32.95) * mm});
            skLineSegment(sketch, "E171", {"start": v(37, 3.95) * mm, "end": v(37, 32.95) * mm});
            skArc(sketch, "E172", {"start": v(40, 32.95) * mm, "mid": v(38.5, 34.45) * mm, "end": v(37, 32.95) * mm});
            skArc(sketch, "E173", {"start": v(37, 3.95) * mm, "mid": v(38.5, 2.45) * mm, "end": v(40, 3.95) * mm});
            skLineSegment(sketch, "E174", {"start": v(44.8, 3.95) * mm, "end": v(44.8, 32.95) * mm});
            skLineSegment(sketch, "E175", {"start": v(41.8, 3.95) * mm, "end": v(41.8, 32.95) * mm});
            skArc(sketch, "E176", {"start": v(44.8, 32.95) * mm, "mid": v(43.3, 34.45) * mm, "end": v(41.8, 32.95) * mm});
            skArc(sketch, "E177", {"start": v(41.8, 3.95) * mm, "mid": v(43.3, 2.45) * mm, "end": v(44.8, 3.95) * mm});
            skLineSegment(sketch, "E178", {"start": v(49.5, 3.95) * mm, "end": v(49.5, 32.95) * mm});
            skLineSegment(sketch, "E179", {"start": v(46.5, 3.95) * mm, "end": v(46.5, 32.95) * mm});
            skArc(sketch, "E180", {"start": v(49.5, 32.95) * mm, "mid": v(48, 34.45) * mm, "end": v(46.5, 32.95) * mm});
            skArc(sketch, "E181", {"start": v(46.5, 3.95) * mm, "mid": v(48, 2.45) * mm, "end": v(49.5, 3.95) * mm});
            skLineSegment(sketch, "E182", {"start": v(54.13, 4.15) * mm, "end": v(54.13, 33.15) * mm});
            skLineSegment(sketch, "E183", {"start": v(51.13, 4.15) * mm, "end": v(51.13, 33.15) * mm});
            skArc(sketch, "E184", {"start": v(54.13, 33.15) * mm, "mid": v(52.63, 34.65) * mm, "end": v(51.13, 33.15) * mm});
            skArc(sketch, "E185", {"start": v(51.13, 4.15) * mm, "mid": v(52.63, 2.65) * mm, "end": v(54.13, 4.15) * mm});
            skLineSegment(sketch, "E186", {"start": v(58.93, 4.15) * mm, "end": v(58.93, 33.15) * mm});
            skLineSegment(sketch, "E187", {"start": v(55.93, 4.15) * mm, "end": v(55.93, 33.15) * mm});
            skArc(sketch, "E188", {"start": v(58.93, 33.15) * mm, "mid": v(57.43, 34.65) * mm, "end": v(55.93, 33.15) * mm});
            skArc(sketch, "E189", {"start": v(55.93, 4.15) * mm, "mid": v(57.43, 2.65) * mm, "end": v(58.93, 4.15) * mm});
            skLineSegment(sketch, "E190", {"start": v(63.63, 4.15) * mm, "end": v(63.63, 33.15) * mm});
            skLineSegment(sketch, "E191", {"start": v(60.63, 4.15) * mm, "end": v(60.63, 33.15) * mm});
            skArc(sketch, "E192", {"start": v(63.63, 33.15) * mm, "mid": v(62.13, 34.65) * mm, "end": v(60.63, 33.15) * mm});
            skArc(sketch, "E193", {"start": v(60.63, 4.15) * mm, "mid": v(62.13, 2.65) * mm, "end": v(63.63, 4.15) * mm});
            skSolve(sketch);
        }
        {
            var Q0;
            Q0=makeQuery(id+"F15.opExtrude","SWEPT_FACE",FACE,{"disambiguationData":[OSD([sQuery(id+"F0.wireOp",EDGE,"E1.0")])]});
            var sketch = newSketch(context, id + "F24", { "sketchPlane" : qUnion([Q0])});
            skLineSegment(sketch, "E194", {"start": v(-60.62, 4.13) * mm, "end": v(-60.62, 33.13) * mm});
            skLineSegment(sketch, "E195", {"start": v(-63.62, 4.13) * mm, "end": v(-63.62, 33.13) * mm});
            skArc(sketch, "E196", {"start": v(-60.62, 33.13) * mm, "mid": v(-62.12, 34.63) * mm, "end": v(-63.62, 33.13) * mm});
            skArc(sketch, "E197", {"start": v(-63.62, 4.13) * mm, "mid": v(-62.12, 2.63) * mm, "end": v(-60.62, 4.13) * mm});
            skLineSegment(sketch, "E198", {"start": v(-55.94, 4.13) * mm, "end": v(-55.94, 33.13) * mm});
            skLineSegment(sketch, "E199", {"start": v(-58.94, 4.13) * mm, "end": v(-58.94, 33.13) * mm});
            skArc(sketch, "E200", {"start": v(-55.94, 33.13) * mm, "mid": v(-57.44, 34.63) * mm, "end": v(-58.94, 33.13) * mm});
            skArc(sketch, "E201", {"start": v(-58.94, 4.13) * mm, "mid": v(-57.44, 2.63) * mm, "end": v(-55.94, 4.13) * mm});
            skLineSegment(sketch, "E202", {"start": v(-51.12, 4.13) * mm, "end": v(-51.12, 33.13) * mm});
            skLineSegment(sketch, "E203", {"start": v(-54.12, 4.13) * mm, "end": v(-54.12, 33.13) * mm});
            skArc(sketch, "E204", {"start": v(-51.12, 33.13) * mm, "mid": v(-52.62, 34.63) * mm, "end": v(-54.12, 33.13) * mm});
            skArc(sketch, "E205", {"start": v(-54.12, 4.13) * mm, "mid": v(-52.62, 2.63) * mm, "end": v(-51.12, 4.13) * mm});
            skLineSegment(sketch, "E206", {"start": v(-46.5, 3.95) * mm, "end": v(-46.5, 32.95) * mm});
            skLineSegment(sketch, "E207", {"start": v(-49.5, 3.95) * mm, "end": v(-49.5, 32.95) * mm});
            skArc(sketch, "E208", {"start": v(-46.5, 32.95) * mm, "mid": v(-48, 34.45) * mm, "end": v(-49.5, 32.95) * mm});
            skArc(sketch, "E209", {"start": v(-49.5, 3.95) * mm, "mid": v(-48, 2.45) * mm, "end": v(-46.5, 3.95) * mm});
            skLineSegment(sketch, "E210", {"start": v(-41.8, 3.95) * mm, "end": v(-41.8, 32.95) * mm});
            skLineSegment(sketch, "E211", {"start": v(-44.8, 3.95) * mm, "end": v(-44.8, 32.95) * mm});
            skArc(sketch, "E212", {"start": v(-41.8, 32.95) * mm, "mid": v(-43.3, 34.45) * mm, "end": v(-44.8, 32.95) * mm});
            skArc(sketch, "E213", {"start": v(-44.8, 3.95) * mm, "mid": v(-43.3, 2.45) * mm, "end": v(-41.8, 3.95) * mm});
            skLineSegment(sketch, "E214", {"start": v(-37, 3.95) * mm, "end": v(-37, 32.95) * mm});
            skLineSegment(sketch, "E215", {"start": v(-40, 3.95) * mm, "end": v(-40, 32.95) * mm});
            skArc(sketch, "E216", {"start": v(-37, 32.95) * mm, "mid": v(-38.5, 34.45) * mm, "end": v(-40, 32.95) * mm});
            skArc(sketch, "E217", {"start": v(-40, 3.95) * mm, "mid": v(-38.5, 2.45) * mm, "end": v(-37, 3.95) * mm});
            skLineSegment(sketch, "E218", {"start": v(-31.98, 3.95) * mm, "end": v(-31.98, 32.95) * mm});
            skLineSegment(sketch, "E219", {"start": v(-34.98, 3.95) * mm, "end": v(-34.98, 32.95) * mm});
            skArc(sketch, "E220", {"start": v(-31.98, 32.95) * mm, "mid": v(-33.48, 34.45) * mm, "end": v(-34.98, 32.95) * mm});
            skArc(sketch, "E221", {"start": v(-34.98, 3.95) * mm, "mid": v(-33.48, 2.45) * mm, "end": v(-31.98, 3.95) * mm});
            skLineSegment(sketch, "E222", {"start": v(-27.28, 3.95) * mm, "end": v(-27.28, 32.95) * mm});
            skLineSegment(sketch, "E223", {"start": v(-30.28, 3.95) * mm, "end": v(-30.28, 32.95) * mm});
            skArc(sketch, "E224", {"start": v(-27.28, 32.95) * mm, "mid": v(-28.78, 34.45) * mm, "end": v(-30.28, 32.95) * mm});
            skArc(sketch, "E225", {"start": v(-30.28, 3.95) * mm, "mid": v(-28.78, 2.45) * mm, "end": v(-27.28, 3.95) * mm});
            skLineSegment(sketch, "E226", {"start": v(-22.48, 3.95) * mm, "end": v(-22.48, 32.95) * mm});
            skLineSegment(sketch, "E227", {"start": v(-25.48, 3.95) * mm, "end": v(-25.48, 32.95) * mm});
            skArc(sketch, "E228", {"start": v(-22.48, 32.95) * mm, "mid": v(-23.98, 34.45) * mm, "end": v(-25.48, 32.95) * mm});
            skArc(sketch, "E229", {"start": v(-25.48, 3.95) * mm, "mid": v(-23.98, 2.45) * mm, "end": v(-22.48, 3.95) * mm});
            skSolve(sketch);
        }
        {
            var Q0;
            Q0 = qSketchRegion(id + "F23", true);
            extrude(context, id + "F25", {"entities" : qUnion([Q0]), "operationType" : NewBodyOperationType.REMOVE, "oppositeDirection" : true, "depth" : 25 * mm});
        }
        {
            var Q0;
            Q0 = qSketchRegion(id + "F24", true);
            extrude(context, id + "F26", {"entities" : qUnion([Q0]), "operationType" : NewBodyOperationType.REMOVE, "oppositeDirection" : true, "depth" : 25 * mm});
        }
        {
            var Q0;
            Q0 = qSketchRegion(id + "F1", true);
            extrude(context, id + "F27", {"entities" : qUnion([Q0]), "depth" : 38 * mm});
        }
    });
